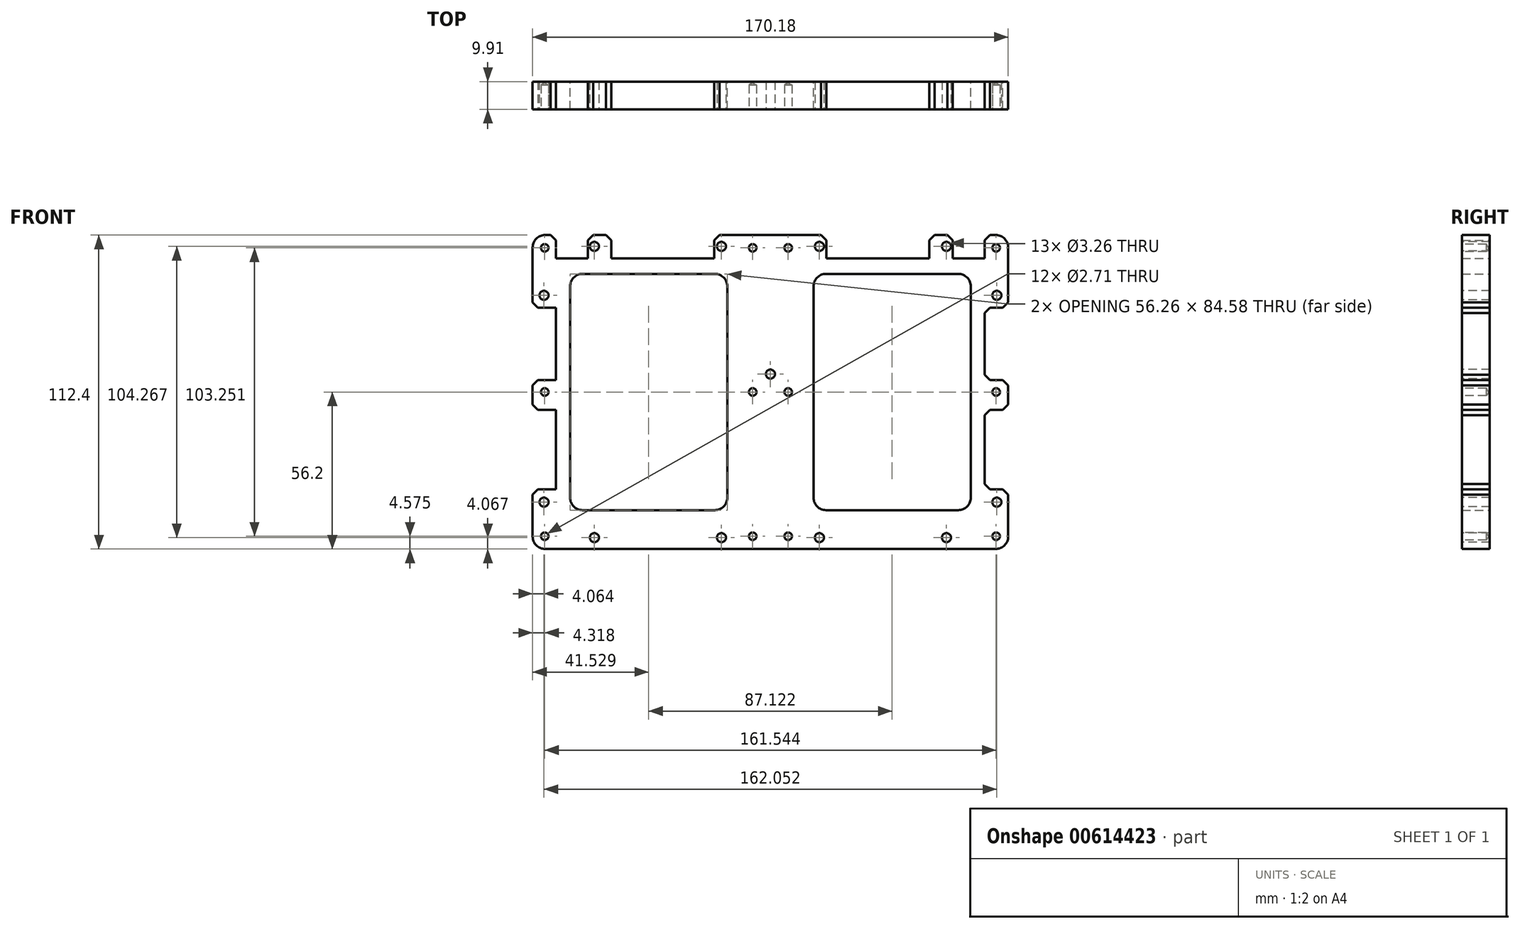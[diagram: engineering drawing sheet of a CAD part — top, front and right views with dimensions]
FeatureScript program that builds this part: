
annotation { "Feature Type Name" : "Feature", "Feature Type Description" : "" }
export const myFeature = defineFeature(function(context is Context, id is Id, definition is map)
    precondition{}
    {
        {
            var Q0;
            Q0=qCreatedBy(makeId("Front.planeOp"),FACE);
            var sketch = newSketch(context, id + "F0", { "sketchPlane" : qUnion([Q0])});
            skLineSegment(sketch, "E0.bottom", {"start": v(-80.64, -56.2) * mm, "end": v(80.64, -56.2) * mm});
            skLineSegment(sketch, "E0.top", {"start": v(-80.65, 56.2) * mm, "end": v(80.65, 56.2) * mm});
            skLineSegment(sketch, "E0.left", {"start": v(-85.09, -51.75) * mm, "end": v(-85.1, 51.75) * mm});
            skLineSegment(sketch, "E0.right", {"start": v(85.1, -56.2) * mm, "end": v(85.1, 56.2) * mm});
            skPoint(sketch, "E0.middle", {"position": v(0, 0) * mm});
            skLineSegment(sketch, "E1.bottom", {"start": v(-85.1, -34.86) * mm, "end": v(-76.7, -34.86) * mm});
            skLineSegment(sketch, "E1.top", {"start": v(-85.1, -6.41) * mm, "end": v(-76.7, -6.41) * mm});
            skLineSegment(sketch, "E1.left", {"start": v(-85.09, -34.86) * mm, "end": v(-85.09, -6.41) * mm});
            skLineSegment(sketch, "E1.right", {"start": v(-76.7, -34.86) * mm, "end": v(-76.7, -6.41) * mm});
            skLineSegment(sketch, "E2.bottom", {"start": v(-85.1, 4.25) * mm, "end": v(-76.7, 4.25) * mm});
            skLineSegment(sketch, "E2.top", {"start": v(-85.1, 30.16) * mm, "end": v(-76.7, 30.16) * mm});
            skLineSegment(sketch, "E2.left", {"start": v(-85.1, 4.25) * mm, "end": v(-85.1, 30.16) * mm});
            skLineSegment(sketch, "E2.right", {"start": v(-76.7, 4.25) * mm, "end": v(-76.7, 30.16) * mm});
            skLineSegment(sketch, "E3.bottom", {"start": v(-76.7, 56.2) * mm, "end": v(-65.28, 56.2) * mm});
            skLineSegment(sketch, "E3.top", {"start": v(-76.7, 47.82) * mm, "end": v(-65.28, 47.82) * mm});
            skLineSegment(sketch, "E3.left", {"start": v(-76.7, 56.2) * mm, "end": v(-76.7, 47.82) * mm});
            skLineSegment(sketch, "E3.right", {"start": v(-65.28, 56.2) * mm, "end": v(-65.28, 47.82) * mm});
            skPoint(sketch, "E4.oppositeSnap0", {"position": v(-71, 47.82) * mm});
            skLineSegment(sketch, "E4.bottom", {"start": v(-56.9, 56.2) * mm, "end": v(-20.07, 56.2) * mm});
            skLineSegment(sketch, "E4.top", {"start": v(-56.9, 47.82) * mm, "end": v(-20.07, 47.82) * mm});
            skLineSegment(sketch, "E4.left", {"start": v(-56.9, 56.2) * mm, "end": v(-56.9, 47.82) * mm});
            skLineSegment(sketch, "E4.right", {"start": v(-20.07, 56.2) * mm, "end": v(-20.07, 47.82) * mm});
            skLineSegment(sketch, "E5.bottom", {"start": v(-19.88, -42.3) * mm, "end": v(-67.25, -42.3) * mm});
            skLineSegment(sketch, "E5.top", {"start": v(-19.88, 42.3) * mm, "end": v(-67.25, 42.3) * mm});
            skLineSegment(sketch, "E5.left", {"start": v(-15.43, -37.85) * mm, "end": v(-15.43, 37.85) * mm});
            skLineSegment(sketch, "E5.right", {"start": v(-71.7, -37.85) * mm, "end": v(-71.7, 37.85) * mm});
            skPoint(sketch, "E5.middle", {"position": v(-43.56, 0) * mm});
            skPoint(sketch, "E6.visualSharp", {"position": v(-71.7, 42.3) * mm});
            skArc(sketch, "E6.filletArc", {"start": v(-67.25, 42.3) * mm, "mid": v(-70.39, 40.99) * mm, "end": v(-71.7, 37.85) * mm});
            skPoint(sketch, "E7.visualSharp", {"position": v(-15.43, 42.3) * mm});
            skArc(sketch, "E7.filletArc", {"start": v(-15.43, 37.85) * mm, "mid": v(-16.73, 40.99) * mm, "end": v(-19.88, 42.3) * mm});
            skPoint(sketch, "E8.visualSharp", {"position": v(-15.43, -42.3) * mm});
            skArc(sketch, "E8.filletArc", {"start": v(-19.88, -42.3) * mm, "mid": v(-16.73, -40.99) * mm, "end": v(-15.43, -37.85) * mm});
            skPoint(sketch, "E9.visualSharp", {"position": v(-71.7, -42.3) * mm});
            skArc(sketch, "E9.filletArc", {"start": v(-71.7, -37.85) * mm, "mid": v(-70.39, -40.99) * mm, "end": v(-67.25, -42.3) * mm});
            skArc(sketch, "E10.MirrorCS", {"start": v(71.7, -37.85) * mm, "mid": v(70.39, -40.99) * mm, "end": v(67.25, -42.3) * mm});
            skArc(sketch, "E11.MirrorCS", {"start": v(67.25, 42.3) * mm, "mid": v(70.39, 40.99) * mm, "end": v(71.7, 37.85) * mm});
            skLineSegment(sketch, "E12.MirrorCS", {"start": v(76.7, 47.82) * mm, "end": v(65.28, 47.82) * mm});
            skArc(sketch, "E13.MirrorCS", {"start": v(19.88, -42.3) * mm, "mid": v(16.73, -40.99) * mm, "end": v(15.43, -37.85) * mm});
            skArc(sketch, "E14.MirrorCS", {"start": v(15.43, 37.85) * mm, "mid": v(16.73, 40.99) * mm, "end": v(19.88, 42.3) * mm});
            skLineSegment(sketch, "E15.MirrorCS", {"start": v(65.28, 56.2) * mm, "end": v(65.28, 47.82) * mm});
            skLineSegment(sketch, "E16.MirrorCS", {"start": v(85.1, -6.41) * mm, "end": v(76.7, -6.41) * mm});
            skLineSegment(sketch, "E17.MirrorCS", {"start": v(56.9, 47.82) * mm, "end": v(20.07, 47.82) * mm});
            skPoint(sketch, "E18.MirrorP", {"position": v(71.7, 42.3) * mm});
            skLineSegment(sketch, "E19.MirrorCS", {"start": v(20.07, 56.2) * mm, "end": v(20.07, 47.82) * mm});
            skLineSegment(sketch, "E20.MirrorCS", {"start": v(56.9, 56.2) * mm, "end": v(20.07, 56.2) * mm});
            skLineSegment(sketch, "E21.MirrorCS", {"start": v(19.88, -42.3) * mm, "end": v(67.25, -42.3) * mm});
            skLineSegment(sketch, "E22.MirrorCS", {"start": v(71.7, -37.85) * mm, "end": v(71.7, 37.85) * mm});
            skPoint(sketch, "E23.MirrorP", {"position": v(71.7, -42.3) * mm});
            skLineSegment(sketch, "E24.MirrorCS", {"start": v(76.7, 56.2) * mm, "end": v(65.28, 56.2) * mm});
            skLineSegment(sketch, "E25.MirrorCS", {"start": v(76.7, 4.25) * mm, "end": v(76.7, 30.16) * mm});
            skLineSegment(sketch, "E26.MirrorCS", {"start": v(85.1, 4.25) * mm, "end": v(85.1, 30.16) * mm});
            skLineSegment(sketch, "E27.MirrorCS", {"start": v(85.1, 30.16) * mm, "end": v(76.7, 30.16) * mm});
            skLineSegment(sketch, "E28.MirrorCS", {"start": v(85.1, 4.25) * mm, "end": v(76.7, 4.25) * mm});
            skLineSegment(sketch, "E29.MirrorCS", {"start": v(76.7, -34.86) * mm, "end": v(76.7, -6.41) * mm});
            skLineSegment(sketch, "E30.MirrorCS", {"start": v(85.09, -34.86) * mm, "end": v(85.09, -6.41) * mm});
            skPoint(sketch, "E31.MirrorP", {"position": v(15.43, -42.3) * mm});
            skLineSegment(sketch, "E32.MirrorCS", {"start": v(85.1, -34.86) * mm, "end": v(76.7, -34.86) * mm});
            skLineSegment(sketch, "E33.MirrorCS", {"start": v(85.09, -51.75) * mm, "end": v(85.1, 51.75) * mm});
            skLineSegment(sketch, "E34.MirrorCS", {"start": v(76.7, 56.2) * mm, "end": v(76.7, 47.82) * mm});
            skLineSegment(sketch, "E35.MirrorCS", {"start": v(19.88, 42.3) * mm, "end": v(67.25, 42.3) * mm});
            skLineSegment(sketch, "E36.MirrorCS", {"start": v(15.43, -37.85) * mm, "end": v(15.43, 37.85) * mm});
            skPoint(sketch, "E37.MirrorP", {"position": v(71, 47.82) * mm});
            skLineSegment(sketch, "E38.MirrorCS", {"start": v(56.9, 56.2) * mm, "end": v(56.9, 47.82) * mm});
            skPoint(sketch, "E39.MirrorP", {"position": v(15.43, 42.3) * mm});
            skPoint(sketch, "E40.MirrorP", {"position": v(43.56, 0) * mm});
            skPoint(sketch, "E41.visualSharp", {"position": v(-85.1, 56.2) * mm});
            skArc(sketch, "E41.filletArc", {"start": v(-80.65, 56.2) * mm, "mid": v(-83.79, 54.9) * mm, "end": v(-85.1, 51.75) * mm});
            skPoint(sketch, "E42.visualSharp", {"position": v(-85.09, -56.2) * mm});
            skArc(sketch, "E42.filletArc", {"start": v(-85.09, -51.75) * mm, "mid": v(-83.79, -54.9) * mm, "end": v(-80.64, -56.2) * mm});
            skPoint(sketch, "E43.visualSharp", {"position": v(85.1, -56.2) * mm});
            skArc(sketch, "E43.filletArc", {"start": v(80.64, -56.2) * mm, "mid": v(83.79, -54.9) * mm, "end": v(85.09, -51.75) * mm});
            skPoint(sketch, "E44.visualSharp", {"position": v(85.09, 56.2) * mm});
            skArc(sketch, "E44.filletArc", {"start": v(85.1, 51.75) * mm, "mid": v(83.79, 54.9) * mm, "end": v(80.65, 56.2) * mm});
            skSolve(sketch);
        }
        {
            var Q0;
            {var subQ12=sQuery(id+"F0.wireOp",EDGE,"E0.bottom");Q0=makeQuery(id+"F0.imprint","IMPRINT",FACE,{"disambiguationData":[TD([[makeQuery(id+"F0.imprint","IMPRINT",EDGE,{"derivedFrom":subQ12}),1.0]])]});}
            extrude(context, id + "F1", {"entities" : qUnion([Q0]), "depth" : 9.9 * mm});
        }
        {
            var Q0;
            Q0=makeQuery(id+"F1.opExtrude","SWEPT_EDGE",EDGE,{"disambiguationData":[OSD([sQuery(id+"F0.wireOp",EDGE,"E0.left"),sQuery(id+"F0.wireOp",EDGE,"E1.bottom"),sQuery(id+"F0.wireOp",EDGE,"E1.left")])]});
            var Q1;
            Q1=makeQuery(id+"F1.opExtrude","SWEPT_EDGE",EDGE,{"disambiguationData":[OSD([sQuery(id+"F0.wireOp",EDGE,"E0.left"),sQuery(id+"F0.wireOp",EDGE,"E1.top"),sQuery(id+"F0.wireOp",EDGE,"E1.left")])]});
            var Q2;
            Q2=makeQuery(id+"F1.opExtrude","SWEPT_EDGE",EDGE,{"disambiguationData":[OSD([sQuery(id+"F0.wireOp",EDGE,"E0.left"),sQuery(id+"F0.wireOp",EDGE,"E2.bottom"),sQuery(id+"F0.wireOp",EDGE,"E2.left")])]});
            var Q3;
            Q3=makeQuery(id+"F1.opExtrude","SWEPT_EDGE",EDGE,{"disambiguationData":[OSD([sQuery(id+"F0.wireOp",EDGE,"E0.left"),sQuery(id+"F0.wireOp",EDGE,"E2.top"),sQuery(id+"F0.wireOp",EDGE,"E2.left")])]});
            var Q4;
            Q4=makeQuery(id+"F1.opExtrude","SWEPT_EDGE",EDGE,{"disambiguationData":[OSD([sQuery(id+"F0.wireOp",EDGE,"E0.top"),sQuery(id+"F0.wireOp",EDGE,"E3.bottom"),sQuery(id+"F0.wireOp",EDGE,"E3.left")])]});
            var Q5;
            Q5=makeQuery(id+"F1.opExtrude","SWEPT_EDGE",EDGE,{"disambiguationData":[OSD([sQuery(id+"F0.wireOp",EDGE,"E0.top"),sQuery(id+"F0.wireOp",EDGE,"E3.bottom"),sQuery(id+"F0.wireOp",EDGE,"E3.right")])]});
            var Q6;
            Q6=makeQuery(id+"F1.opExtrude","SWEPT_EDGE",EDGE,{"disambiguationData":[OSD([sQuery(id+"F0.wireOp",EDGE,"E0.top"),sQuery(id+"F0.wireOp",EDGE,"E4.bottom"),sQuery(id+"F0.wireOp",EDGE,"E4.left")])]});
            var Q7;
            Q7=makeQuery(id+"F1.opExtrude","SWEPT_EDGE",EDGE,{"disambiguationData":[OSD([sQuery(id+"F0.wireOp",EDGE,"E0.top"),sQuery(id+"F0.wireOp",EDGE,"E4.bottom"),sQuery(id+"F0.wireOp",EDGE,"E4.right")])]});
            var Q8;
            Q8=makeQuery(id+"F1.opExtrude","SWEPT_EDGE",EDGE,{"disambiguationData":[OSD([sQuery(id+"F0.wireOp",EDGE,"E0.top"),sQuery(id+"F0.wireOp",EDGE,"E19.MirrorCS"),sQuery(id+"F0.wireOp",EDGE,"E20.MirrorCS")])]});
            var Q9;
            Q9=makeQuery(id+"F1.opExtrude","SWEPT_EDGE",EDGE,{"disambiguationData":[OSD([sQuery(id+"F0.wireOp",EDGE,"E0.top"),sQuery(id+"F0.wireOp",EDGE,"E15.MirrorCS"),sQuery(id+"F0.wireOp",EDGE,"E24.MirrorCS")])]});
            var Q10;
            Q10=makeQuery(id+"F1.opExtrude","SWEPT_EDGE",EDGE,{"disambiguationData":[OSD([sQuery(id+"F0.wireOp",EDGE,"E0.top"),sQuery(id+"F0.wireOp",EDGE,"E20.MirrorCS"),sQuery(id+"F0.wireOp",EDGE,"E38.MirrorCS")])]});
            var Q11;
            Q11=makeQuery(id+"F1.opExtrude","SWEPT_EDGE",EDGE,{"disambiguationData":[OSD([sQuery(id+"F0.wireOp",EDGE,"E0.top"),sQuery(id+"F0.wireOp",EDGE,"E24.MirrorCS"),sQuery(id+"F0.wireOp",EDGE,"E34.MirrorCS")])]});
            var Q12;
            Q12=makeQuery(id+"F1.opExtrude","SWEPT_EDGE",EDGE,{"disambiguationData":[OSD([sQuery(id+"F0.wireOp",EDGE,"E27.MirrorCS"),sQuery(id+"F0.wireOp",EDGE,"E33.MirrorCS")])]});
            var Q13;
            Q13=makeQuery(id+"F1.opExtrude","SWEPT_EDGE",EDGE,{"disambiguationData":[OSD([sQuery(id+"F0.wireOp",EDGE,"E28.MirrorCS"),sQuery(id+"F0.wireOp",EDGE,"E33.MirrorCS")])]});
            var Q14;
            Q14=makeQuery(id+"F1.opExtrude","SWEPT_EDGE",EDGE,{"disambiguationData":[OSD([sQuery(id+"F0.wireOp",EDGE,"E16.MirrorCS"),sQuery(id+"F0.wireOp",EDGE,"E33.MirrorCS")])]});
            var Q15;
            Q15=makeQuery(id+"F1.opExtrude","SWEPT_EDGE",EDGE,{"disambiguationData":[OSD([sQuery(id+"F0.wireOp",EDGE,"E32.MirrorCS"),sQuery(id+"F0.wireOp",EDGE,"E33.MirrorCS")])]});
            chamfer(context, id + "F2", {"entities" : qUnion([Q0, Q1, Q2, Q3, Q4, Q5, Q6, Q7, Q8, Q9, Q10, Q11, Q12, Q13, Q14, Q15]), "width" : 1.9 * mm, "tangentPropagation" : true});
        }
        {
            var Q0;
            Q0=makeQuery(id+"F1.opExtrude","CAP_FACE",FACE,{"disambiguationData":[OSD([sQuery(id+"F0.wireOp",EDGE,"E0.bottom"),sQuery(id+"F0.wireOp",EDGE,"E0.top"),sQuery(id+"F0.wireOp",EDGE,"E0.left"),sQuery(id+"F0.wireOp",EDGE,"E1.bottom"),sQuery(id+"F0.wireOp",EDGE,"E1.top"),sQuery(id+"F0.wireOp",EDGE,"E1.right"),sQuery(id+"F0.wireOp",EDGE,"E2.bottom"),sQuery(id+"F0.wireOp",EDGE,"E2.top"),sQuery(id+"F0.wireOp",EDGE,"E2.right"),sQuery(id+"F0.wireOp",EDGE,"E3.top"),sQuery(id+"F0.wireOp",EDGE,"E3.left"),sQuery(id+"F0.wireOp",EDGE,"E3.right"),sQuery(id+"F0.wireOp",EDGE,"E4.top"),sQuery(id+"F0.wireOp",EDGE,"E4.left"),sQuery(id+"F0.wireOp",EDGE,"E4.right"),sQuery(id+"F0.wireOp",EDGE,"E5.bottom"),sQuery(id+"F0.wireOp",EDGE,"E5.top"),sQuery(id+"F0.wireOp",EDGE,"E5.left"),sQuery(id+"F0.wireOp",EDGE,"E5.right"),sQuery(id+"F0.wireOp",EDGE,"E6.filletArc"),sQuery(id+"F0.wireOp",EDGE,"E7.filletArc"),sQuery(id+"F0.wireOp",EDGE,"E8.filletArc"),sQuery(id+"F0.wireOp",EDGE,"E9.filletArc"),sQuery(id+"F0.wireOp",EDGE,"E10.MirrorCS"),sQuery(id+"F0.wireOp",EDGE,"E11.MirrorCS"),sQuery(id+"F0.wireOp",EDGE,"E12.MirrorCS"),sQuery(id+"F0.wireOp",EDGE,"E13.MirrorCS"),sQuery(id+"F0.wireOp",EDGE,"E14.MirrorCS"),sQuery(id+"F0.wireOp",EDGE,"E15.MirrorCS"),sQuery(id+"F0.wireOp",EDGE,"E16.MirrorCS"),sQuery(id+"F0.wireOp",EDGE,"E17.MirrorCS"),sQuery(id+"F0.wireOp",EDGE,"E19.MirrorCS"),sQuery(id+"F0.wireOp",EDGE,"E21.MirrorCS"),sQuery(id+"F0.wireOp",EDGE,"E22.MirrorCS"),sQuery(id+"F0.wireOp",EDGE,"E25.MirrorCS"),sQuery(id+"F0.wireOp",EDGE,"E27.MirrorCS"),sQuery(id+"F0.wireOp",EDGE,"E28.MirrorCS"),sQuery(id+"F0.wireOp",EDGE,"E29.MirrorCS"),sQuery(id+"F0.wireOp",EDGE,"E32.MirrorCS"),sQuery(id+"F0.wireOp",EDGE,"E33.MirrorCS"),sQuery(id+"F0.wireOp",EDGE,"E34.MirrorCS"),sQuery(id+"F0.wireOp",EDGE,"E35.MirrorCS"),sQuery(id+"F0.wireOp",EDGE,"E36.MirrorCS"),sQuery(id+"F0.wireOp",EDGE,"E38.MirrorCS"),sQuery(id+"F0.wireOp",EDGE,"E41.filletArc"),sQuery(id+"F0.wireOp",EDGE,"E42.filletArc"),sQuery(id+"F0.wireOp",EDGE,"E43.filletArc"),sQuery(id+"F0.wireOp",EDGE,"E44.filletArc")])],"isStart":false});
            var sketch = newSketch(context, id + "F3", { "sketchPlane" : qUnion([Q0])});
            skPoint(sketch, "E45", {"position": v(-80.77, 51.63) * mm});
            skPoint(sketch, "E46", {"position": v(-80.77, 0) * mm});
            skPoint(sketch, "E47", {"position": v(-80.77, -51.63) * mm});
            skPoint(sketch, "E48", {"position": v(-6.35, -51.63) * mm});
            skPoint(sketch, "E49", {"position": v(-6.35, 0) * mm});
            skPoint(sketch, "E50", {"position": v(-6.35, 51.63) * mm});
            skPoint(sketch, "E51.MirrorP", {"position": v(80.77, -51.63) * mm});
            skPoint(sketch, "E52.MirrorP", {"position": v(80.77, 51.63) * mm});
            skPoint(sketch, "E53.MirrorP", {"position": v(6.35, 51.63) * mm});
            skPoint(sketch, "E54.MirrorP", {"position": v(6.35, -51.63) * mm});
            skPoint(sketch, "E55.MirrorP", {"position": v(6.35, 0) * mm});
            skPoint(sketch, "E56.MirrorP", {"position": v(80.77, 0) * mm});
            skSolve(sketch);
        }
        {
            var Q0;
            Q0=sQuery(id+"F3.wireOp",VERTEX,"E45");
            var Q1;
            Q1=sQuery(id+"F3.wireOp",VERTEX,"E46");
            var Q2;
            Q2=sQuery(id+"F3.wireOp",VERTEX,"E47");
            var Q3;
            Q3=sQuery(id+"F3.wireOp",VERTEX,"E48");
            var Q4;
            Q4=sQuery(id+"F3.wireOp",VERTEX,"E49");
            var Q5;
            Q5=sQuery(id+"F3.wireOp",VERTEX,"E50");
            var Q6;
            Q6=sQuery(id+"F3.wireOp",VERTEX,"E53.MirrorP");
            var Q7;
            Q7=sQuery(id+"F3.wireOp",VERTEX,"E55.MirrorP");
            var Q8;
            Q8=sQuery(id+"F3.wireOp",VERTEX,"E54.MirrorP");
            var Q9;
            Q9=sQuery(id+"F3.wireOp",VERTEX,"E51.MirrorP");
            var Q10;
            Q10=sQuery(id+"F3.wireOp",VERTEX,"E56.MirrorP");
            var Q11;
            Q11=sQuery(id+"F3.wireOp",VERTEX,"E52.MirrorP");
            var Q12;
            Q12=makeQuery(id+"F1.opExtrude","SWEPT_BODY",BODY,{"disambiguationData":[OSD([sQuery(id+"F0.wireOp",EDGE,"E0.bottom"),sQuery(id+"F0.wireOp",EDGE,"E0.top"),sQuery(id+"F0.wireOp",EDGE,"E0.left"),sQuery(id+"F0.wireOp",EDGE,"E1.bottom"),sQuery(id+"F0.wireOp",EDGE,"E1.top"),sQuery(id+"F0.wireOp",EDGE,"E1.right"),sQuery(id+"F0.wireOp",EDGE,"E2.bottom"),sQuery(id+"F0.wireOp",EDGE,"E2.top"),sQuery(id+"F0.wireOp",EDGE,"E2.right"),sQuery(id+"F0.wireOp",EDGE,"E3.top"),sQuery(id+"F0.wireOp",EDGE,"E3.left"),sQuery(id+"F0.wireOp",EDGE,"E3.right"),sQuery(id+"F0.wireOp",EDGE,"E4.top"),sQuery(id+"F0.wireOp",EDGE,"E4.left"),sQuery(id+"F0.wireOp",EDGE,"E4.right"),sQuery(id+"F0.wireOp",EDGE,"E5.bottom"),sQuery(id+"F0.wireOp",EDGE,"E5.top"),sQuery(id+"F0.wireOp",EDGE,"E5.left"),sQuery(id+"F0.wireOp",EDGE,"E5.right"),sQuery(id+"F0.wireOp",EDGE,"E6.filletArc"),sQuery(id+"F0.wireOp",EDGE,"E7.filletArc"),sQuery(id+"F0.wireOp",EDGE,"E8.filletArc"),sQuery(id+"F0.wireOp",EDGE,"E9.filletArc"),sQuery(id+"F0.wireOp",EDGE,"E10.MirrorCS"),sQuery(id+"F0.wireOp",EDGE,"E11.MirrorCS"),sQuery(id+"F0.wireOp",EDGE,"E12.MirrorCS"),sQuery(id+"F0.wireOp",EDGE,"E13.MirrorCS"),sQuery(id+"F0.wireOp",EDGE,"E14.MirrorCS"),sQuery(id+"F0.wireOp",EDGE,"E15.MirrorCS"),sQuery(id+"F0.wireOp",EDGE,"E16.MirrorCS"),sQuery(id+"F0.wireOp",EDGE,"E17.MirrorCS"),sQuery(id+"F0.wireOp",EDGE,"E19.MirrorCS"),sQuery(id+"F0.wireOp",EDGE,"E21.MirrorCS"),sQuery(id+"F0.wireOp",EDGE,"E22.MirrorCS"),sQuery(id+"F0.wireOp",EDGE,"E25.MirrorCS"),sQuery(id+"F0.wireOp",EDGE,"E27.MirrorCS"),sQuery(id+"F0.wireOp",EDGE,"E28.MirrorCS"),sQuery(id+"F0.wireOp",EDGE,"E29.MirrorCS"),sQuery(id+"F0.wireOp",EDGE,"E32.MirrorCS"),sQuery(id+"F0.wireOp",EDGE,"E33.MirrorCS"),sQuery(id+"F0.wireOp",EDGE,"E34.MirrorCS"),sQuery(id+"F0.wireOp",EDGE,"E35.MirrorCS"),sQuery(id+"F0.wireOp",EDGE,"E36.MirrorCS"),sQuery(id+"F0.wireOp",EDGE,"E38.MirrorCS"),sQuery(id+"F0.wireOp",EDGE,"E41.filletArc"),sQuery(id+"F0.wireOp",EDGE,"E42.filletArc"),sQuery(id+"F0.wireOp",EDGE,"E43.filletArc"),sQuery(id+"F0.wireOp",EDGE,"E44.filletArc")])]});
            hole(context, id + "F4", {"style" : HoleStyle.SIMPLE, "endStyle" : HoleEndStyle.BLIND, "standardTappedOrClearance" : lookupTablePath({ "standard" : "ANSI", "engagement" : "75%", "pitch" : "32 tpi", "size" : "#6", "type" : "Tapped" }), "standardBlindInLast" : lookupTablePath({ "standard" : "ANSI", "engagement" : "75%", "pitch" : "32 tpi", "size" : "#6", "type" : "Tapped" }), "holeDiameter" : 2.7 * mm, "showTappedDepth" : true, "holeDepth" : 8.73 * mm, "tappedDepth" : 6.35 * mm, "tapClearance" : 3, "locations" : qUnion([Q0, Q1, Q2, Q3, Q4, Q5, Q6, Q7, Q8, Q9, Q10, Q11]), "scope" : qUnion([Q12]), "majorDiameter" : 3.5 * mm});
        }
        {
            var Q0;
            Q0=makeQuery(id+"F1.opExtrude","CAP_FACE",FACE,{"disambiguationData":[OSD([sQuery(id+"F0.wireOp",EDGE,"E0.bottom"),sQuery(id+"F0.wireOp",EDGE,"E0.top"),sQuery(id+"F0.wireOp",EDGE,"E0.left"),sQuery(id+"F0.wireOp",EDGE,"E1.bottom"),sQuery(id+"F0.wireOp",EDGE,"E1.top"),sQuery(id+"F0.wireOp",EDGE,"E1.right"),sQuery(id+"F0.wireOp",EDGE,"E2.bottom"),sQuery(id+"F0.wireOp",EDGE,"E2.top"),sQuery(id+"F0.wireOp",EDGE,"E2.right"),sQuery(id+"F0.wireOp",EDGE,"E3.top"),sQuery(id+"F0.wireOp",EDGE,"E3.left"),sQuery(id+"F0.wireOp",EDGE,"E3.right"),sQuery(id+"F0.wireOp",EDGE,"E4.top"),sQuery(id+"F0.wireOp",EDGE,"E4.left"),sQuery(id+"F0.wireOp",EDGE,"E4.right"),sQuery(id+"F0.wireOp",EDGE,"E5.bottom"),sQuery(id+"F0.wireOp",EDGE,"E5.top"),sQuery(id+"F0.wireOp",EDGE,"E5.left"),sQuery(id+"F0.wireOp",EDGE,"E5.right"),sQuery(id+"F0.wireOp",EDGE,"E6.filletArc"),sQuery(id+"F0.wireOp",EDGE,"E7.filletArc"),sQuery(id+"F0.wireOp",EDGE,"E8.filletArc"),sQuery(id+"F0.wireOp",EDGE,"E9.filletArc"),sQuery(id+"F0.wireOp",EDGE,"E10.MirrorCS"),sQuery(id+"F0.wireOp",EDGE,"E11.MirrorCS"),sQuery(id+"F0.wireOp",EDGE,"E12.MirrorCS"),sQuery(id+"F0.wireOp",EDGE,"E13.MirrorCS"),sQuery(id+"F0.wireOp",EDGE,"E14.MirrorCS"),sQuery(id+"F0.wireOp",EDGE,"E15.MirrorCS"),sQuery(id+"F0.wireOp",EDGE,"E16.MirrorCS"),sQuery(id+"F0.wireOp",EDGE,"E17.MirrorCS"),sQuery(id+"F0.wireOp",EDGE,"E19.MirrorCS"),sQuery(id+"F0.wireOp",EDGE,"E21.MirrorCS"),sQuery(id+"F0.wireOp",EDGE,"E22.MirrorCS"),sQuery(id+"F0.wireOp",EDGE,"E25.MirrorCS"),sQuery(id+"F0.wireOp",EDGE,"E27.MirrorCS"),sQuery(id+"F0.wireOp",EDGE,"E28.MirrorCS"),sQuery(id+"F0.wireOp",EDGE,"E29.MirrorCS"),sQuery(id+"F0.wireOp",EDGE,"E32.MirrorCS"),sQuery(id+"F0.wireOp",EDGE,"E33.MirrorCS"),sQuery(id+"F0.wireOp",EDGE,"E34.MirrorCS"),sQuery(id+"F0.wireOp",EDGE,"E35.MirrorCS"),sQuery(id+"F0.wireOp",EDGE,"E36.MirrorCS"),sQuery(id+"F0.wireOp",EDGE,"E38.MirrorCS"),sQuery(id+"F0.wireOp",EDGE,"E41.filletArc"),sQuery(id+"F0.wireOp",EDGE,"E42.filletArc"),sQuery(id+"F0.wireOp",EDGE,"E43.filletArc"),sQuery(id+"F0.wireOp",EDGE,"E44.filletArc")])],"isStart":false});
            var sketch = newSketch(context, id + "F5", { "sketchPlane" : qUnion([Q0])});
            skPoint(sketch, "E57", {"position": v(0, 6.41) * mm});
            skPoint(sketch, "E58", {"position": v(-17.53, 52.13) * mm});
            skPoint(sketch, "E59", {"position": v(-63, 52.13) * mm});
            skPoint(sketch, "E60", {"position": v(-81.03, 34.6) * mm});
            skPoint(sketch, "E61", {"position": v(-81.03, -39.43) * mm});
            skPoint(sketch, "E62", {"position": v(-63, -52.13) * mm});
            skPoint(sketch, "E63", {"position": v(-17.53, -52.13) * mm});
            skPoint(sketch, "E64.MirrorP", {"position": v(17.53, 52.13) * mm});
            skPoint(sketch, "E65.MirrorP", {"position": v(81.03, -39.43) * mm});
            skPoint(sketch, "E66.MirrorP", {"position": v(81.03, 34.6) * mm});
            skPoint(sketch, "E67.MirrorP", {"position": v(17.53, -52.13) * mm});
            skPoint(sketch, "E68.MirrorP", {"position": v(63, -52.13) * mm});
            skPoint(sketch, "E69.MirrorP", {"position": v(63, 52.13) * mm});
            skSolve(sketch);
        }
        {
            var Q0;
            Q0=sQuery(id+"F5.wireOp",VERTEX,"E60");
            var Q1;
            Q1=sQuery(id+"F5.wireOp",VERTEX,"E59");
            var Q2;
            Q2=sQuery(id+"F5.wireOp",VERTEX,"E61");
            var Q3;
            Q3=sQuery(id+"F5.wireOp",VERTEX,"E62");
            var Q4;
            Q4=sQuery(id+"F5.wireOp",VERTEX,"E58");
            var Q5;
            Q5=sQuery(id+"F5.wireOp",VERTEX,"E63");
            var Q6;
            Q6=sQuery(id+"F5.wireOp",VERTEX,"E57");
            var Q7;
            Q7=sQuery(id+"F5.wireOp",VERTEX,"E67.MirrorP");
            var Q8;
            Q8=sQuery(id+"F5.wireOp",VERTEX,"E68.MirrorP");
            var Q9;
            Q9=sQuery(id+"F5.wireOp",VERTEX,"E65.MirrorP");
            var Q10;
            Q10=sQuery(id+"F5.wireOp",VERTEX,"E66.MirrorP");
            var Q11;
            Q11=sQuery(id+"F5.wireOp",VERTEX,"E69.MirrorP");
            var Q12;
            Q12=sQuery(id+"F5.wireOp",VERTEX,"E64.MirrorP");
            var Q13;
            Q13=makeQuery(id+"F1.opExtrude","SWEPT_BODY",BODY,{"disambiguationData":[OSD([sQuery(id+"F0.wireOp",EDGE,"E0.bottom"),sQuery(id+"F0.wireOp",EDGE,"E0.top"),sQuery(id+"F0.wireOp",EDGE,"E0.left"),sQuery(id+"F0.wireOp",EDGE,"E1.bottom"),sQuery(id+"F0.wireOp",EDGE,"E1.top"),sQuery(id+"F0.wireOp",EDGE,"E1.right"),sQuery(id+"F0.wireOp",EDGE,"E2.bottom"),sQuery(id+"F0.wireOp",EDGE,"E2.top"),sQuery(id+"F0.wireOp",EDGE,"E2.right"),sQuery(id+"F0.wireOp",EDGE,"E3.top"),sQuery(id+"F0.wireOp",EDGE,"E3.left"),sQuery(id+"F0.wireOp",EDGE,"E3.right"),sQuery(id+"F0.wireOp",EDGE,"E4.top"),sQuery(id+"F0.wireOp",EDGE,"E4.left"),sQuery(id+"F0.wireOp",EDGE,"E4.right"),sQuery(id+"F0.wireOp",EDGE,"E5.bottom"),sQuery(id+"F0.wireOp",EDGE,"E5.top"),sQuery(id+"F0.wireOp",EDGE,"E5.left"),sQuery(id+"F0.wireOp",EDGE,"E5.right"),sQuery(id+"F0.wireOp",EDGE,"E6.filletArc"),sQuery(id+"F0.wireOp",EDGE,"E7.filletArc"),sQuery(id+"F0.wireOp",EDGE,"E8.filletArc"),sQuery(id+"F0.wireOp",EDGE,"E9.filletArc"),sQuery(id+"F0.wireOp",EDGE,"E10.MirrorCS"),sQuery(id+"F0.wireOp",EDGE,"E11.MirrorCS"),sQuery(id+"F0.wireOp",EDGE,"E12.MirrorCS"),sQuery(id+"F0.wireOp",EDGE,"E13.MirrorCS"),sQuery(id+"F0.wireOp",EDGE,"E14.MirrorCS"),sQuery(id+"F0.wireOp",EDGE,"E15.MirrorCS"),sQuery(id+"F0.wireOp",EDGE,"E16.MirrorCS"),sQuery(id+"F0.wireOp",EDGE,"E17.MirrorCS"),sQuery(id+"F0.wireOp",EDGE,"E19.MirrorCS"),sQuery(id+"F0.wireOp",EDGE,"E21.MirrorCS"),sQuery(id+"F0.wireOp",EDGE,"E22.MirrorCS"),sQuery(id+"F0.wireOp",EDGE,"E25.MirrorCS"),sQuery(id+"F0.wireOp",EDGE,"E27.MirrorCS"),sQuery(id+"F0.wireOp",EDGE,"E28.MirrorCS"),sQuery(id+"F0.wireOp",EDGE,"E29.MirrorCS"),sQuery(id+"F0.wireOp",EDGE,"E32.MirrorCS"),sQuery(id+"F0.wireOp",EDGE,"E33.MirrorCS"),sQuery(id+"F0.wireOp",EDGE,"E34.MirrorCS"),sQuery(id+"F0.wireOp",EDGE,"E35.MirrorCS"),sQuery(id+"F0.wireOp",EDGE,"E36.MirrorCS"),sQuery(id+"F0.wireOp",EDGE,"E38.MirrorCS"),sQuery(id+"F0.wireOp",EDGE,"E41.filletArc"),sQuery(id+"F0.wireOp",EDGE,"E42.filletArc"),sQuery(id+"F0.wireOp",EDGE,"E43.filletArc"),sQuery(id+"F0.wireOp",EDGE,"E44.filletArc")])]});
            hole(context, id + "F6", {"style" : HoleStyle.SIMPLE, "endStyle" : HoleEndStyle.THROUGH, "standardTappedOrClearance" : lookupTablePath({ "standard" : "ANSI", "fit" : "Normal (ASME)", "size" : "#4", "type" : "Clearance" }), "standardBlindInLast" : lookupTablePath({ "fit" : "Free", "standard" : "ANSI", "size" : "#4", "type" : "Clearance" }), "holeDiameter" : 3.26 * mm, "tappedDepth" : 6.36 * mm, "tapClearance" : 3, "locations" : qUnion([Q0, Q1, Q2, Q3, Q4, Q5, Q6, Q7, Q8, Q9, Q10, Q11, Q12]), "scope" : qUnion([Q13])});
        }
    });
